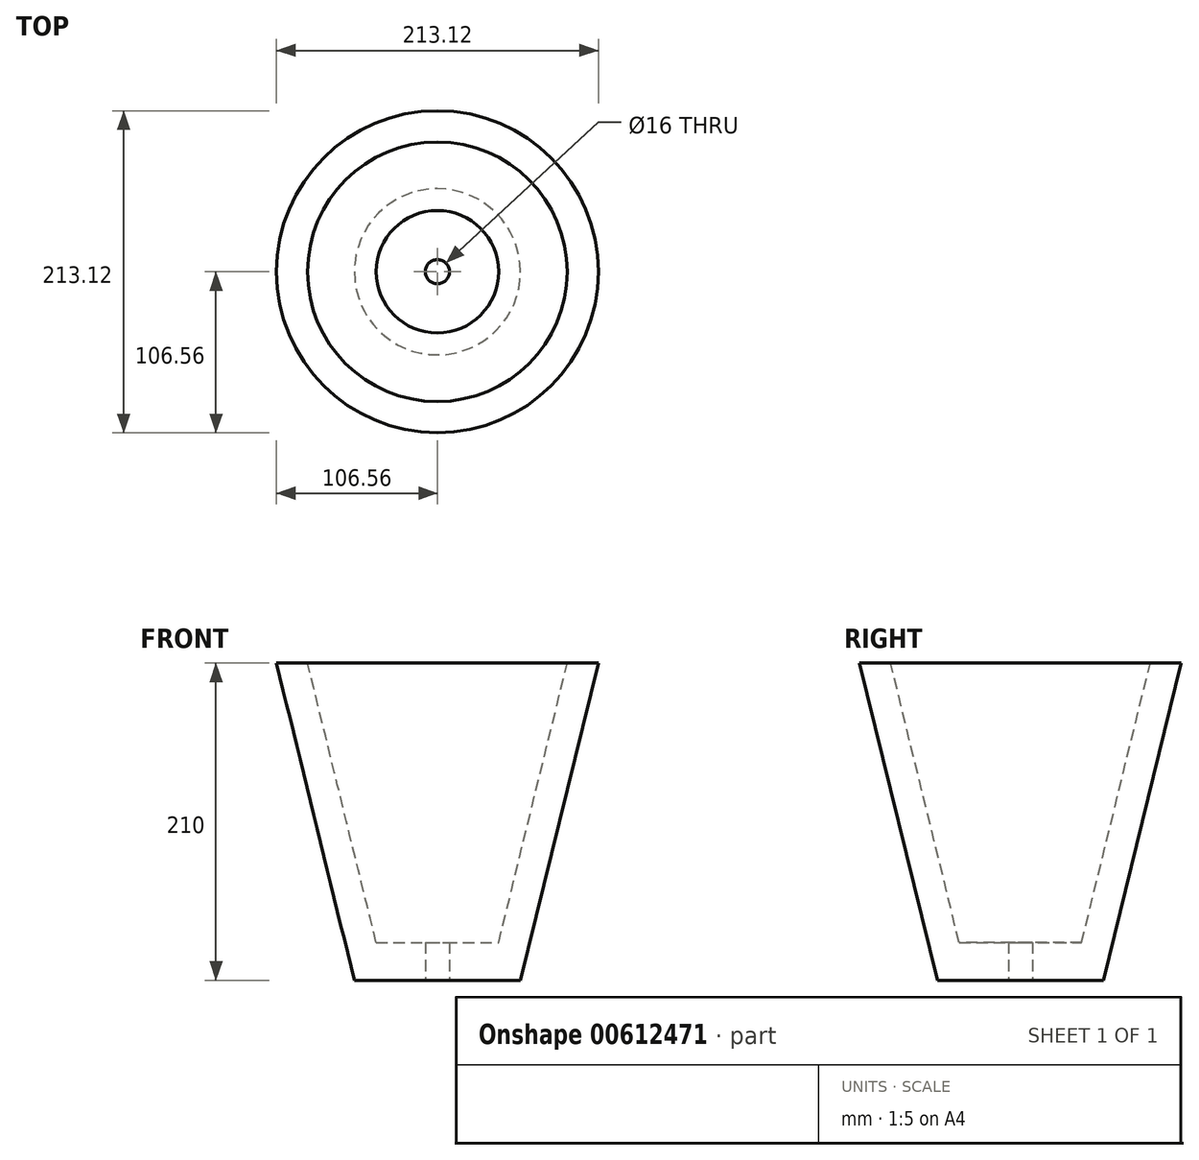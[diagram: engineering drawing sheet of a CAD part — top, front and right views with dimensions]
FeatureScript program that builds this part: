
annotation { "Feature Type Name" : "Feature", "Feature Type Description" : "" }
export const myFeature = defineFeature(function(context is Context, id is Id, definition is map)
    precondition{}
    {
        {
            var Q0;
            Q0=qCreatedBy(makeId("Right.planeOp"),FACE);
            var sketch = newSketch(context, id + "F0", { "sketchPlane" : qUnion([Q0])});
            skLineSegment(sketch, "E0", {"start": v(0, 0) * mm, "end": v(0, 210) * mm});
            skSolve(sketch);
        }
        {
            var Q0;
            Q0=qCreatedBy(makeId("Front.planeOp"),FACE);
            var sketch = newSketch(context, id + "F1", { "sketchPlane" : qUnion([Q0])});
            skLineSegment(sketch, "E1", {"start": v(0, 0) * mm, "end": v(-55, 0) * mm});
            skLineSegment(sketch, "E2", {"start": v(-55, 0) * mm, "end": v(-106.56, 210) * mm});
            skLineSegment(sketch, "E3", {"start": v(-106.56, 210) * mm, "end": v(-85.96, 210) * mm});
            skLineSegment(sketch, "E4", {"start": v(-85.96, 210) * mm, "end": v(-40.54, 25) * mm});
            skLineSegment(sketch, "E5", {"start": v(-40.54, 25) * mm, "end": v(0, 25) * mm});
            skLineSegment(sketch, "E6", {"start": v(0, 25) * mm, "end": v(0, 0) * mm});
            skSolve(sketch);
        }
        {
            var Q0;
            Q0 = qSketchRegion(id + "F1", true);
            var Q1;
            Q1=sQuery(id+"F0.wireOp",EDGE,"E0");
            revolve(context, id + "F2", {"entities" : qUnion([Q0]), "axis" : qUnion([Q1]), "revolveType" : RevolveType.FULL});
        }
        {
            var Q0;
            Q0=makeQuery(id+"F2.opRevolve","SWEPT_FACE",FACE,{"disambiguationData":[OSD([sQuery(id+"F1.wireOp",EDGE,"E1")])]});
            var sketch = newSketch(context, id + "F3", { "sketchPlane" : qUnion([Q0])});
            skCircle(sketch, "E7", {"center": v(0, 0) * mm, "radius": 8 * mm});
            skSolve(sketch);
        }
        {
            var Q0;
            Q0 = qSketchRegion(id + "F3", true);
            extrude(context, id + "F4", {"entities" : qUnion([Q0]), "operationType" : NewBodyOperationType.REMOVE, "oppositeDirection" : true, "depth" : 25 * mm, "offsetDistance" : 25 * mm});
        }
    });
